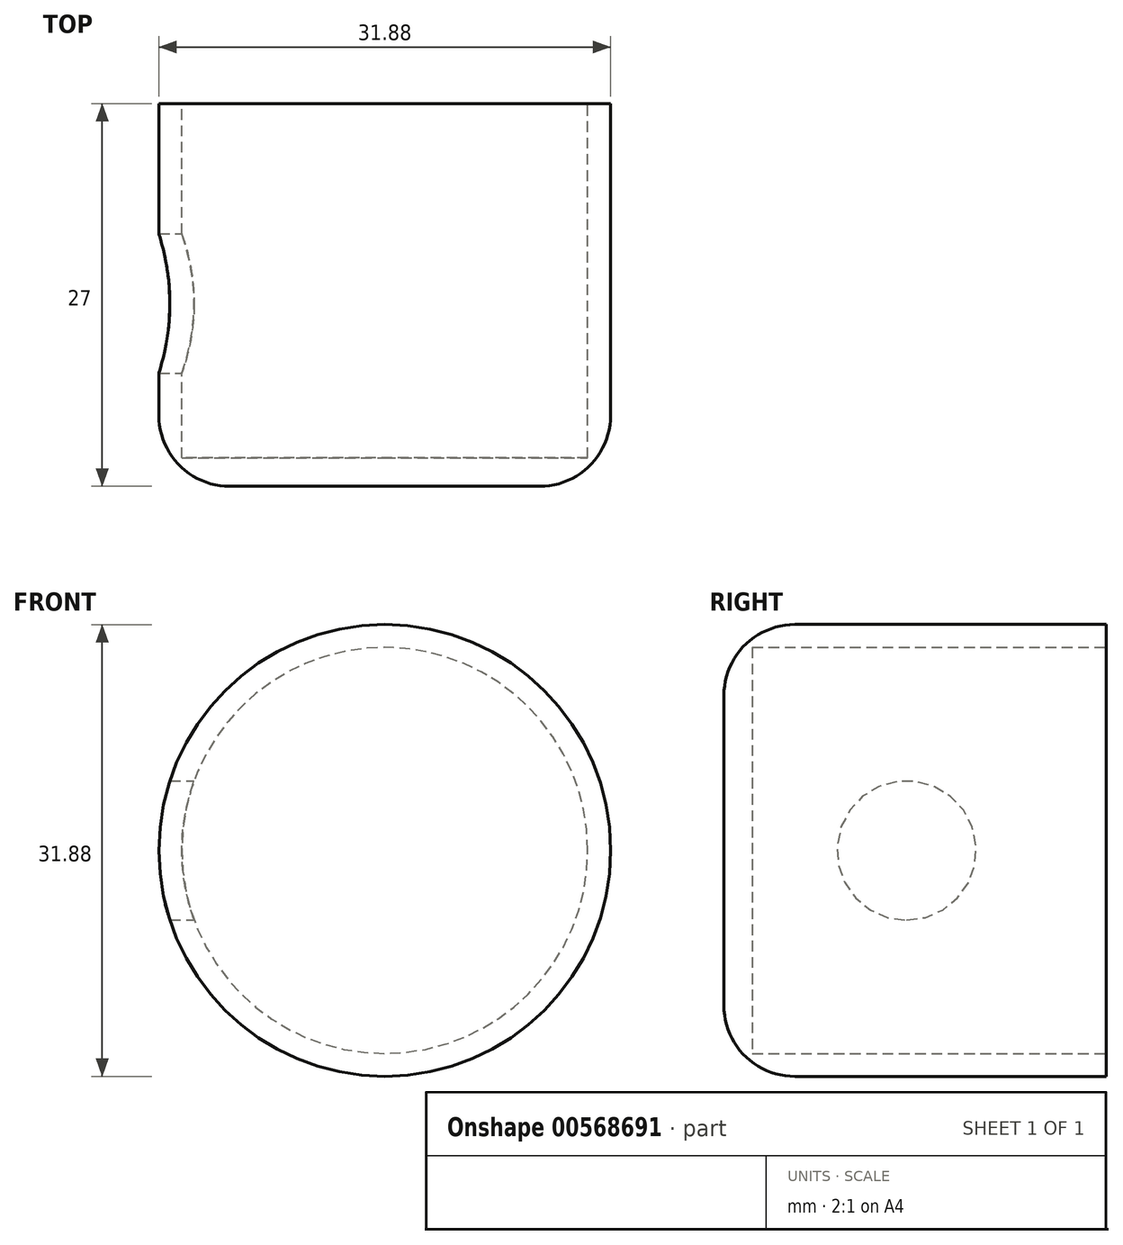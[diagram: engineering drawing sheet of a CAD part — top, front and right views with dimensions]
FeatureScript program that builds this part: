
annotation { "Feature Type Name" : "Feature", "Feature Type Description" : "" }
export const myFeature = defineFeature(function(context is Context, id is Id, definition is map)
    precondition{}
    {
        {
            var Q0;
            Q0=qCreatedBy(makeId("Front.planeOp"),FACE);
            var sketch = newSketch(context, id + "F0", { "sketchPlane" : qUnion([Q0])});
            skCircle(sketch, "E0", {"center": v(0, 0) * mm, "radius": 15.94 * mm});
            skSolve(sketch);
        }
        {
            var Q0;
            Q0=makeQuery(id+"F0.imprint","IMPRINT",FACE,{"disambiguationData":[TD([[makeQuery(id+"F0.imprint","IMPRINT",EDGE,{"derivedFrom":sQuery(id+"F0.wireOp",EDGE,"E0")}),1.0]])]});
            var sketch = newSketch(context, id + "F1", { "sketchPlane" : qUnion([Q0])});
            skCircle(sketch, "E1", {"center": v(0, 0) * mm, "radius": 14 * mm});
            skSolve(sketch);
        }
        {
            var Q0;
            Q0=makeQuery(id+"F0.imprint","IMPRINT",FACE,{"disambiguationData":[TD([[makeQuery(id+"F0.imprint","IMPRINT",EDGE,{"derivedFrom":sQuery(id+"F0.wireOp",EDGE,"E0")}),1.0]])]});
            var Q1;
            Q1=sQuery(id+"F0.wireOp",EDGE,"E0");
            extrude(context, id + "F2", {"entities" : qUnion([Q0]), "surfaceEntities" : qUnion([Q1]), "depth" : 12 * mm, "offsetDistance" : 25 * mm});
        }
        {
            var Q0;
            Q0 = qSketchRegion(id + "F1", true);
            extrude(context, id + "F3", {"entities" : qUnion([Q0]), "operationType" : NewBodyOperationType.REMOVE, "endBound" : BoundingType.THROUGH_ALL, "oppositeDirection" : true, "depth" : 25 * mm, "offsetDistance" : 25 * mm});
        }
        {
            var Q0;
            Q0=makeQuery(id+"F2.opExtrude","CAP_FACE",FACE,{"disambiguationData":[OSD([sQuery(id+"F0.wireOp",EDGE,"E0")])],"isStart":true});
            extrude(context, id + "F4", {"entities" : qUnion([Q0]), "operationType" : NewBodyOperationType.ADD, "depth" : 15 * mm, "offsetDistance" : 25 * mm});
        }
        {
            var Q0;
            Q0=makeQuery(id+"F4.opExtrude","CAP_FACE",FACE,{"disambiguationData":[OSD([sQuery(id+"F0.wireOp",EDGE,"E0")])],"isStart":false});
            var sketch = newSketch(context, id + "F5", { "sketchPlane" : qUnion([Q0])});
            skCircle(sketch, "E2", {"center": v(0, 0) * mm, "radius": 14.32 * mm});
            skSolve(sketch);
        }
        {
            var Q0;
            Q0=makeQuery(id+"F5.imprint","IMPRINT",FACE,{"disambiguationData":[TD([[makeQuery(id+"F5.imprint","IMPRINT",EDGE,{"derivedFrom":sQuery(id+"F5.wireOp",EDGE,"E2")}),1.0]])]});
            extrude(context, id + "F6", {"entities" : qUnion([Q0]), "operationType" : NewBodyOperationType.REMOVE, "oppositeDirection" : true, "depth" : 25 * mm, "offsetDistance" : 25 * mm});
        }
        {
            var Q0;
            Q0=makeQuery(id+"F2.opExtrude","CAP_EDGE",EDGE,{"disambiguationData":[OSD([sQuery(id+"F0.wireOp",EDGE,"E0")])],"isStart":false});
            fillet(context, id + "F7", {"entities" : qUnion([Q0]), "radius" : 5 * mm, "tangentPropagation" : true, "allowEdgeOverflow" : false});
        }
        {
            var Q0;
            Q0=qCreatedBy(makeId("Right.planeOp"),FACE);
            var sketch = newSketch(context, id + "F8", { "sketchPlane" : qUnion([Q0])});
            skCircle(sketch, "E3", {"center": v(0.9, 0) * mm, "radius": 4.91 * mm});
            skSolve(sketch);
        }
        {
            var Q0;
            Q0=makeQuery(id+"F8.imprint","IMPRINT",FACE,{"disambiguationData":[TD([[makeQuery(id+"F8.imprint","IMPRINT",EDGE,{"derivedFrom":sQuery(id+"F8.wireOp",EDGE,"E3")}),1.0]])]});
            extrude(context, id + "F9", {"entities" : qUnion([Q0]), "operationType" : NewBodyOperationType.REMOVE, "endBound" : BoundingType.THROUGH_ALL, "oppositeDirection" : true, "depth" : 6 * mm, "offsetDistance" : 25 * mm});
        }
    });
